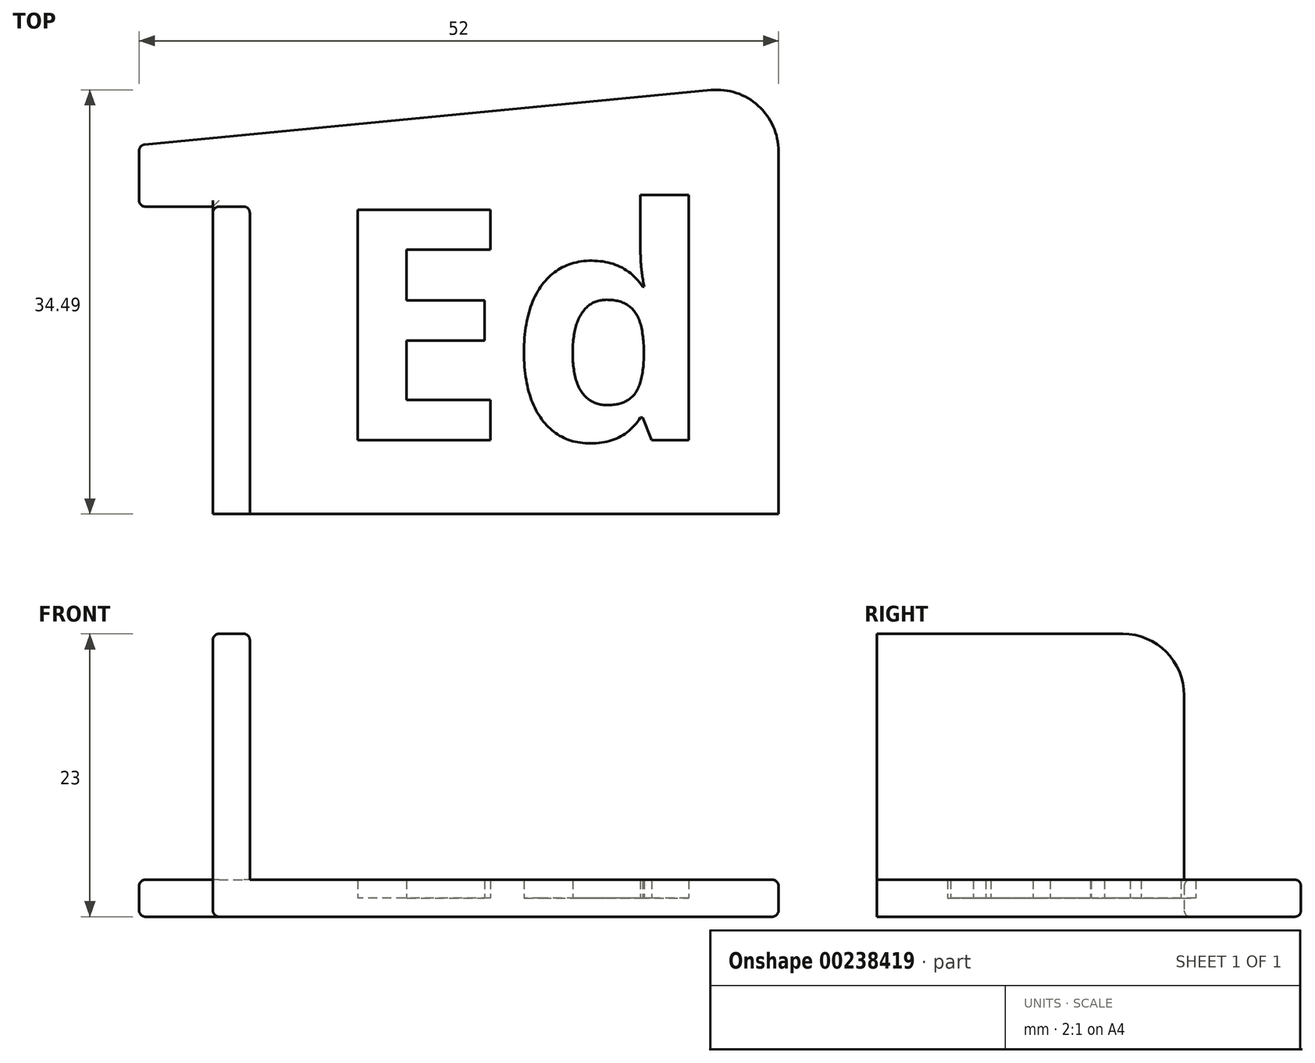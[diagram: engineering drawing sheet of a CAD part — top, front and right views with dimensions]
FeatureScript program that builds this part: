
annotation { "Feature Type Name" : "Feature", "Feature Type Description" : "" }
export const myFeature = defineFeature(function(context is Context, id is Id, definition is map)
    precondition{}
    {
        {
            var Q0;
            Q0=qCreatedBy(makeId("Top.planeOp"),FACE);
            var sketch = newSketch(context, id + "F0", { "sketchPlane" : qUnion([Q0])});
            skLineSegment(sketch, "E0", {"start": v(-20.55, 9.84) * mm, "end": v(-20.55, 4.84) * mm});
            skLineSegment(sketch, "E1", {"start": v(-20.55, 4.84) * mm, "end": v(-14.55, 4.84) * mm});
            skLineSegment(sketch, "E2", {"start": v(-14.55, 4.84) * mm, "end": v(-14.55, -20.16) * mm});
            skLineSegment(sketch, "E3", {"start": v(-14.55, -20.16) * mm, "end": v(31.45, -20.16) * mm});
            skLineSegment(sketch, "E4", {"start": v(31.45, -20.16) * mm, "end": v(31.45, 9.33) * mm});
            skLineSegment(sketch, "E5", {"start": v(-20.55, 9.84) * mm, "end": v(25.97, 14.31) * mm});
            skPoint(sketch, "E6.visualSharp", {"position": v(31.45, 14.84) * mm});
            skArc(sketch, "E6.filletArc", {"start": v(31.45, 9.33) * mm, "mid": v(29.8, 13.03) * mm, "end": v(25.97, 14.31) * mm});
            skLineSegment(sketch, "E7.bottom", {"start": v(-14.55, 4.84) * mm, "end": v(-11.55, 4.84) * mm});
            skLineSegment(sketch, "E7.top", {"start": v(-14.55, -20.16) * mm, "end": v(-11.55, -20.16) * mm});
            skLineSegment(sketch, "E7.right", {"start": v(-11.55, 4.84) * mm, "end": v(-11.55, -20.16) * mm});
            skText(sketch, "E8", { "text": "Ed", "fontName": "OpenSans-Bold.ttf"});
            const initialGuessF0  = {"E8": [-0.00513, -0.01416, 1, 0, 0.0189]};
            skSetInitialGuess(sketch, initialGuessF0);
            skSolve(sketch);
        }
        {
            var Q0;
            Q0=makeQuery(id+"F0.imprint","IMPRINT",FACE,{"disambiguationData":[TD([[makeQuery(id+"F0.imprint","IMPRINT",EDGE,{"derivedFrom":sQuery(id+"F0.wireOp",EDGE,"E0")}),1.0]])]});
            extrude(context, id + "F1", {"entities" : qUnion([Q0]), "depth" : 3 * mm, "offsetDistance" : 25 * mm});
        }
        {
            var Q0;
            {var subQ0=sQuery(id+"F0.wireOp",EDGE,"E2");Q0=makeQuery(id+"F0.imprint","IMPRINT",FACE,{"disambiguationData":[TD([[makeQuery(id+"F0.imprint","IMPRINT",EDGE,{"derivedFrom":subQ0}),1.0]])]});}
            extrude(context, id + "F2", {"entities" : qUnion([Q0]), "operationType" : NewBodyOperationType.ADD, "depth" : 23 * mm, "offsetDistance" : 25 * mm});
        }
        {
            var Q0;
            Q0=makeQuery(id+"F1.opExtrude","CAP_EDGE",EDGE,{"disambiguationData":[OSD([sQuery(id+"F0.wireOp",EDGE,"E5")])],"isStart":true});
            var Q1;
            Q1=makeQuery(id+"F1.opExtrude","CAP_EDGE",EDGE,{"disambiguationData":[OSD([sQuery(id+"F0.wireOp",EDGE,"E5")])],"isStart":false});
            var Q2;
            Q2=makeQuery(id+"F1.opExtrude","SWEPT_EDGE",EDGE,{"disambiguationData":[OSD([sQuery(id+"F0.wireOp",EDGE,"E0"),sQuery(id+"F0.wireOp",EDGE,"E5")])]});
            var Q3;
            Q3=makeQuery(id+"F1.opExtrude","CAP_EDGE",EDGE,{"disambiguationData":[OSD([sQuery(id+"F0.wireOp",EDGE,"E6.filletArc")])],"isStart":false});
            var Q4;
            Q4=makeQuery(id+"F1.opExtrude","CAP_EDGE",EDGE,{"disambiguationData":[OSD([sQuery(id+"F0.wireOp",EDGE,"E4")])],"isStart":false});
            var Q5;
            Q5=makeQuery(id+"F1.opExtrude","CAP_EDGE",EDGE,{"disambiguationData":[OSD([sQuery(id+"F0.wireOp",EDGE,"E6.filletArc")])],"isStart":true});
            var Q6;
            Q6=makeQuery(id+"F1.opExtrude","CAP_EDGE",EDGE,{"disambiguationData":[OSD([sQuery(id+"F0.wireOp",EDGE,"E4")])],"isStart":true});
            fillet(context, id + "F3", {"entities" : qUnion([Q0, Q1, Q2, Q3, Q4, Q5, Q6]), "radius" : .5 * mm, "tangentPropagation" : true, "allowEdgeOverflow" : false});
        }
        {
            var Q0;
            Q0=makeQuery(id+"F1.opExtrude","CAP_EDGE",EDGE,{"disambiguationData":[OSD([sQuery(id+"F0.wireOp",EDGE,"E7.right")])],"isStart":false});
            var Q1;
            {var subQ0=sQuery(id+"F0.wireOp",EDGE,"E7.bottom");var subQ1=sQuery(id+"F0.wireOp",EDGE,"E1");Q1=makeQuery(id+"F2.boolean.opBoolean","SPLIT",EDGE,{"disambiguationData":[topologyDisambiguationEdgeConnected([makeQuery(id+"F2.opExtrude","SWEPT_FACE",FACE,{"disambiguationData":[OSD([subQ0])]})])],"derivedFrom":makeQuery(id+"F1.opExtrude","CAP_EDGE",EDGE,{"disambiguationData":[OSD([subQ1,subQ0])],"isStart":false})});}
            fillet(context, id + "F4", {"entities" : qUnion([Q0, Q1]), "radius" : .5 * mm, "tangentPropagation" : true, "allowEdgeOverflow" : false});
        }
        {
            var Q0;
            Q0=makeQuery(id+"F2.opExtrude","CAP_EDGE",EDGE,{"disambiguationData":[OSD([sQuery(id+"F0.wireOp",EDGE,"E7.right")])],"isStart":false});
            var Q1;
            Q1=makeQuery(id+"F2.opExtrude","SWEPT_EDGE",EDGE,{"disambiguationData":[OSD([sQuery(id+"F0.wireOp",EDGE,"E7.bottom"),sQuery(id+"F0.wireOp",EDGE,"E7.right")])]});
            var Q2;
            Q2=makeQuery(id+"F2.opExtrude","CAP_EDGE",EDGE,{"disambiguationData":[OSD([sQuery(id+"F0.wireOp",EDGE,"E2")])],"isStart":false});
            var Q3;
            {var subQ0=sQuery(id+"F0.wireOp",EDGE,"E2");var subQ1=sQuery(id+"F0.wireOp",EDGE,"E7.bottom");Q3=makeQuery(id+"F2.boolean.opBoolean","SPLIT",EDGE,{"disambiguationData":[topologyDisambiguationEdgeConnected([makeQuery(id+"F2.opExtrude","SWEPT_FACE",FACE,{"disambiguationData":[OSD([subQ1])]})])],"derivedFrom":makeQuery(id+"F2.opExtrude","SWEPT_EDGE",EDGE,{"disambiguationData":[OSD([sQuery(id+"F0.wireOp",EDGE,"E1"),subQ0,subQ1])]})});}
            fillet(context, id + "F5", {"entities" : qUnion([Q0, Q1, Q2, Q3]), "radius" : .5 * mm, "tangentPropagation" : true, "allowEdgeOverflow" : false});
        }
        {
            var Q0;
            Q0=makeQuery(id+"F1.opExtrude","CAP_EDGE",EDGE,{"disambiguationData":[OSD([sQuery(id+"F0.wireOp",EDGE,"E1"),sQuery(id+"F0.wireOp",EDGE,"E7.bottom")])],"isStart":true});
            var Q1;
            Q1=makeQuery(id+"F1.opExtrude","CAP_EDGE",EDGE,{"disambiguationData":[OSD([sQuery(id+"F0.wireOp",EDGE,"E0")])],"isStart":true});
            var Q2;
            {var subQ0=sQuery(id+"F0.wireOp",EDGE,"E7.bottom");var subQ1=sQuery(id+"F0.wireOp",EDGE,"E1");Q2=makeQuery(id+"F2.boolean.opBoolean","SPLIT",EDGE,{"disambiguationData":[topologyDisambiguationEdgeConnected([makeQuery(id+"F1.opExtrude","SWEPT_FACE",FACE,{"disambiguationData":[OSD([subQ1,subQ0])]})])],"derivedFrom":makeQuery(id+"F1.opExtrude","CAP_EDGE",EDGE,{"disambiguationData":[OSD([subQ1,subQ0])],"isStart":false})});}
            var Q3;
            Q3=makeQuery(id+"F1.opExtrude","CAP_EDGE",EDGE,{"disambiguationData":[OSD([sQuery(id+"F0.wireOp",EDGE,"E0")])],"isStart":false});
            var Q4;
            Q4=makeQuery(id+"F1.opExtrude","SWEPT_EDGE",EDGE,{"disambiguationData":[OSD([sQuery(id+"F0.wireOp",EDGE,"E0"),sQuery(id+"F0.wireOp",EDGE,"E1")])]});
            fillet(context, id + "F6", {"entities" : qUnion([Q0, Q1, Q2, Q3, Q4]), "radius" : .5 * mm, "tangentPropagation" : true, "allowEdgeOverflow" : false});
        }
        {
            var Q0;
            Q0=makeQuery(id+"F2.opExtrude","CAP_EDGE",EDGE,{"disambiguationData":[OSD([sQuery(id+"F0.wireOp",EDGE,"E2")])],"isStart":true});
            fillet(context, id + "F7", {"entities" : qUnion([Q0]), "radius" : .5 * mm, "tangentPropagation" : true, "allowEdgeOverflow" : false});
        }
        {
            var Q0;
            Q0=makeQuery(id+"F0.imprint","IMPRINT",FACE,{"disambiguationData":[TD([[makeQuery(id+"F0.imprint","IMPRINT",EDGE,{"derivedFrom":sQuery(id+"F0.wireOp",EDGE,"E8.sketch_text.stroke-0")}),-1.0]])]});
            var Q1;
            Q1=makeQuery(id+"F0.imprint","IMPRINT",FACE,{"disambiguationData":[TD([[makeQuery(id+"F0.imprint","IMPRINT",EDGE,{"derivedFrom":sQuery(id+"F0.wireOp",EDGE,"E8.sketch_text.stroke-12")}),-1.0]])]});
            extrude(context, id + "F8", {"entities" : qUnion([Q0, Q1]), "operationType" : NewBodyOperationType.ADD, "depth" : 1.5 * mm, "offsetDistance" : 25 * mm});
        }
        {
            var Q0;
            Q0=makeQuery(id+"F0.imprint","IMPRINT",FACE,{"disambiguationData":[TD([[makeQuery(id+"F0.imprint","IMPRINT",EDGE,{"derivedFrom":sQuery(id+"F0.wireOp",EDGE,"E8.sketch_text.stroke-26")}),1.0]])]});
            extrude(context, id + "F9", {"entities" : qUnion([Q0]), "operationType" : NewBodyOperationType.ADD, "depth" : 3 * mm, "offsetDistance" : 25 * mm});
        }
        {
            var Q0;
            Q0=makeQuery(id+"F2.opExtrude","CAP_EDGE",EDGE,{"disambiguationData":[OSD([sQuery(id+"F0.wireOp",EDGE,"E7.bottom")])],"isStart":false});
            fillet(context, id + "F10", {"entities" : qUnion([Q0]), "radius" : 5 * mm, "tangentPropagation" : true, "allowEdgeOverflow" : false});
        }
    });
